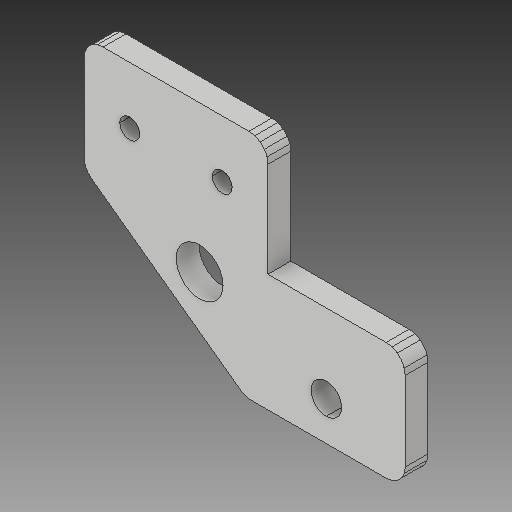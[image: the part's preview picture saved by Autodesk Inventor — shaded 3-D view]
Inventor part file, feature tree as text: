
AUTODESK INVENTOR PART (.ipt)
format: ipt  version: 2018 (Build 220112000, 112)  size: 235,520 bytes
history: native  units: mm
features: other x3, sketch x3
ambient origin geometry x8: Origin, YZ Plane, XZ Plane, XY Plane, X Axis, Y Axis, Z Axis, Center Point
bodies: Solid1 (feature_tree)
feature tree (6):
  other  "Leadscrew-rod-holder_MIR.ipt"
  other  "Solid1::Leadscrew-rod-holder_MIR.ipt"
  other  "TaggingFeature1"
  sketch  "Sketch1"  dims[d0=10.0mm]
  sketch  "Sketch2"
  sketch  "Sketch3"
